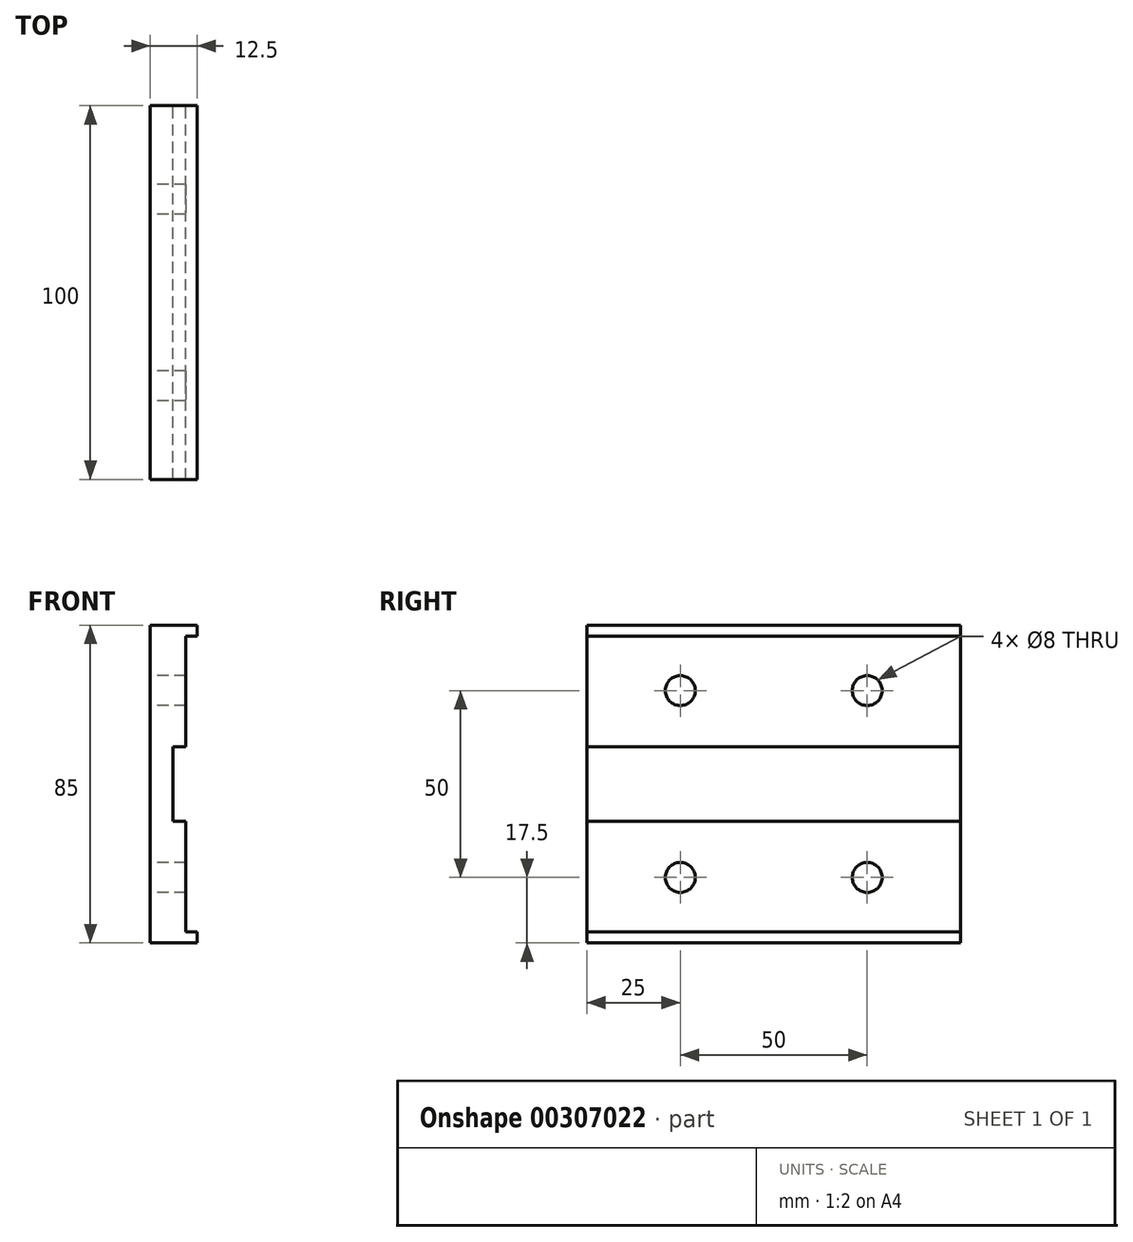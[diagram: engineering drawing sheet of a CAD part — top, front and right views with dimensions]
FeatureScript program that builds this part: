
annotation { "Feature Type Name" : "Feature", "Feature Type Description" : "" }
export const myFeature = defineFeature(function(context is Context, id is Id, definition is map)
    precondition{}
    {
        {
            var Q0;
            Q0=qCreatedBy(makeId("Front.planeOp"),FACE);
            var sketch = newSketch(context, id + "F0", { "sketchPlane" : qUnion([Q0])});
            skLineSegment(sketch, "E0", {"start": v(-19.05, 42.5) * mm, "end": v(-6.55, 42.5) * mm});
            skLineSegment(sketch, "E1", {"start": v(-6.55, 42.5) * mm, "end": v(-6.55, 39.5) * mm});
            skLineSegment(sketch, "E2", {"start": v(-6.55, 39.5) * mm, "end": v(-9.55, 39.5) * mm});
            skLineSegment(sketch, "E3", {"start": v(-9.55, 39.5) * mm, "end": v(-9.55, 10) * mm});
            skLineSegment(sketch, "E4", {"start": v(-9.55, 10) * mm, "end": v(-13.05, 10) * mm});
            skLineSegment(sketch, "E5", {"start": v(-13.05, 10) * mm, "end": v(-13.05, 0) * mm});
            skLineSegment(sketch, "E6", {"start": v(-19.05, 0) * mm, "end": v(-19.05, 42.5) * mm});
            skLineSegment(sketch, "E7.MirrorCS", {"start": v(-9.55, -10) * mm, "end": v(-13.05, -10) * mm});
            skLineSegment(sketch, "E8.MirrorCS", {"start": v(-6.55, -42.5) * mm, "end": v(-6.55, -39.5) * mm});
            skLineSegment(sketch, "E9.MirrorCS", {"start": v(-19.05, -42.5) * mm, "end": v(-6.55, -42.5) * mm});
            skLineSegment(sketch, "E10.MirrorCS", {"start": v(-6.55, -39.5) * mm, "end": v(-9.55, -39.5) * mm});
            skLineSegment(sketch, "E11.MirrorCS", {"start": v(-9.55, -39.5) * mm, "end": v(-9.55, -10) * mm});
            skLineSegment(sketch, "E12.MirrorCS", {"start": v(-13.05, -10) * mm, "end": v(-13.05, 0) * mm});
            skLineSegment(sketch, "E13.MirrorCS", {"start": v(-19.05, 0) * mm, "end": v(-19.05, -42.5) * mm});
            skSolve(sketch);
        }
        {
            var Q0;
            Q0 = qSketchRegion(id + "F0", true);
            extrude(context, id + "F1", {"entities" : qUnion([Q0]), "depth" : 100 * mm});
        }
        {
            var Q0;
            Q0=makeQuery(id+"F1.opExtrude","SWEPT_FACE",FACE,{"disambiguationData":[OSD([sQuery(id+"F0.wireOp",EDGE,"E6"),sQuery(id+"F0.wireOp",EDGE,"E13.MirrorCS")])]});
            var sketch = newSketch(context, id + "F2", { "sketchPlane" : qUnion([Q0])});
            skCircle(sketch, "E14", {"center": v(25, 25) * mm, "radius": 4 * mm});
            skCircle(sketch, "E15", {"center": v(75, 25) * mm, "radius": 4 * mm});
            skCircle(sketch, "E16.MirrorC", {"center": v(25, -25) * mm, "radius": 4 * mm});
            skCircle(sketch, "E17.MirrorC", {"center": v(75, -25) * mm, "radius": 4 * mm});
            skSolve(sketch);
        }
        {
            var Q0;
            Q0 = qSketchRegion(id + "F2", true);
            extrude(context, id + "F3", {"entities" : qUnion([Q0]), "operationType" : NewBodyOperationType.REMOVE, "oppositeDirection" : true, "depth" : 25 * mm});
        }
    });
